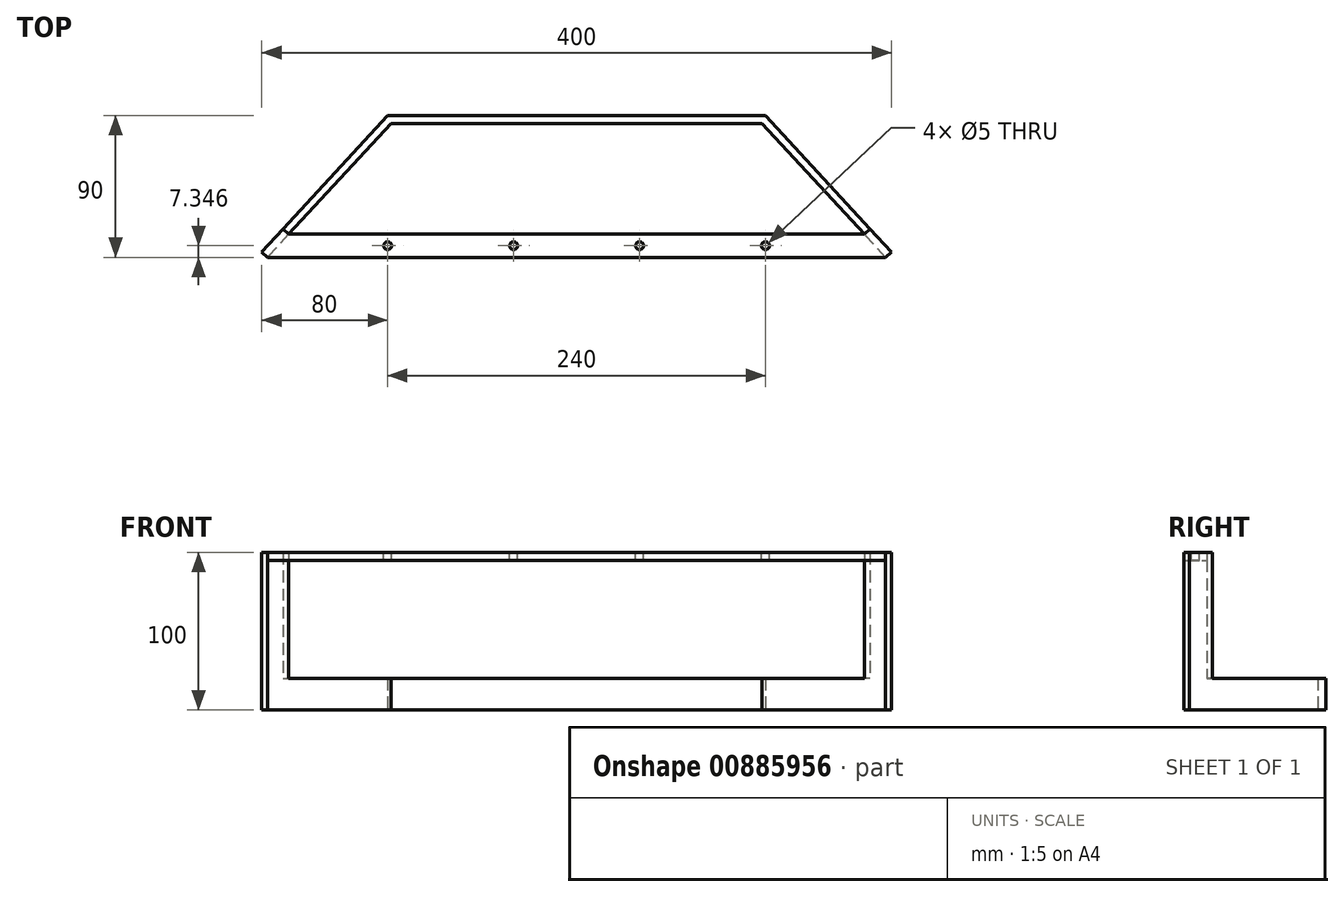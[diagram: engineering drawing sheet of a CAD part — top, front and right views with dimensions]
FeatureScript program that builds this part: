
annotation { "Feature Type Name" : "Feature", "Feature Type Description" : "" }
export const myFeature = defineFeature(function(context is Context, id is Id, definition is map)
    precondition{}
    {
        {
            var Q0;
            Q0=qCreatedBy(makeId("Top.planeOp"),FACE);
            var sketch = newSketch(context, id + "F0", { "sketchPlane" : qUnion([Q0])});
            skLineSegment(sketch, "E0", {"start": v(-200, 3.4) * mm, "end": v(-120, 90) * mm});
            skLineSegment(sketch, "E1", {"start": v(200, 3.4) * mm, "end": v(120, 90) * mm});
            skLineSegment(sketch, "E2", {"start": v(120, 90) * mm, "end": v(-120, 90) * mm});
            skLineSegment(sketch, "E3.0", {"start": v(196.33, 0) * mm, "end": v(117.81, 85) * mm});
            skLineSegment(sketch, "E3.1", {"start": v(117.81, 85) * mm, "end": v(-117.81, 85) * mm});
            skLineSegment(sketch, "E3.2", {"start": v(-196.33, 0) * mm, "end": v(-117.81, 85) * mm});
            skLineSegment(sketch, "E4", {"start": v(-196.33, 0) * mm, "end": v(-200, 3.4) * mm});
            skLineSegment(sketch, "E5", {"start": v(196.33, 0) * mm, "end": v(200, 3.4) * mm});
            skPoint(sketch, "E6.orphan", {"position": v(203.13, 0) * mm});
            skPoint(sketch, "E7.orphan", {"position": v(-203.13, 0) * mm});
            skSolve(sketch);
        }
        {
            var Q0;
            Q0 = qSketchRegion(id + "F0", true);
            extrude(context, id + "F1", {"entities" : qUnion([Q0]), "depth" : 20 * mm, "offsetDistance" : 25 * mm});
        }
        {
            var Q0;
            Q0=makeQuery(id+"F1.opExtrude","CAP_FACE",FACE,{"disambiguationData":[OSD([sQuery(id+"F0.wireOp",EDGE,"E0"),sQuery(id+"F0.wireOp",EDGE,"E1"),sQuery(id+"F0.wireOp",EDGE,"E2"),sQuery(id+"F0.wireOp",EDGE,"E3.0"),sQuery(id+"F0.wireOp",EDGE,"E3.1"),sQuery(id+"F0.wireOp",EDGE,"E3.2"),sQuery(id+"F0.wireOp",EDGE,"E4"),sQuery(id+"F0.wireOp",EDGE,"E5")])],"isStart":false});
            var sketch = newSketch(context, id + "F2", { "sketchPlane" : qUnion([Q0])});
            skLineSegment(sketch, "E8", {"start": v(-200, 3.4) * mm, "end": v(-186.43, 18.08) * mm});
            skLineSegment(sketch, "E9", {"start": v(-186.43, 18.08) * mm, "end": v(-182.76, 14.7) * mm});
            skLineSegment(sketch, "E10", {"start": v(-182.76, 14.7) * mm, "end": v(-196.33, 0) * mm});
            skLineSegment(sketch, "E11.0", {"start": v(-196.33, 0) * mm, "end": v(-200, 3.4) * mm});
            skLineSegment(sketch, "E12.MirrorCS", {"start": v(196.33, 0) * mm, "end": v(200, 3.4) * mm});
            skLineSegment(sketch, "E13.MirrorCS", {"start": v(186.43, 18.08) * mm, "end": v(182.76, 14.7) * mm});
            skLineSegment(sketch, "E14.MirrorCS", {"start": v(182.76, 14.7) * mm, "end": v(196.33, 0) * mm});
            skLineSegment(sketch, "E15.MirrorCS", {"start": v(200, 3.4) * mm, "end": v(186.43, 18.08) * mm});
            skSolve(sketch);
        }
        {
            var Q0;
            Q0=makeQuery(id+"F2.imprint","IMPRINT",FACE,{"disambiguationData":[TD([[makeQuery(id+"F2.imprint","IMPRINT",EDGE,{"derivedFrom":sQuery(id+"F2.wireOp",EDGE,"E8")}),-1.0]])]});
            var Q1;
            Q1=makeQuery(id+"F2.imprint","IMPRINT",FACE,{"disambiguationData":[TD([[makeQuery(id+"F2.imprint","IMPRINT",EDGE,{"derivedFrom":sQuery(id+"F2.wireOp",EDGE,"E12.MirrorCS")}),1.0]])]});
            extrude(context, id + "F3", {"entities" : qUnion([Q0, Q1]), "operationType" : NewBodyOperationType.ADD, "depth" : 80 * mm, "offsetDistance" : 25 * mm});
        }
        {
            var Q0;
            Q0=makeQuery(id+"F3.opExtrude","CAP_FACE",FACE,{"disambiguationData":[OSD([sQuery(id+"F2.wireOp",EDGE,"E12.MirrorCS"),sQuery(id+"F2.wireOp",EDGE,"E13.MirrorCS"),sQuery(id+"F2.wireOp",EDGE,"E14.MirrorCS"),sQuery(id+"F2.wireOp",EDGE,"E15.MirrorCS")])],"isStart":false});
            var sketch = newSketch(context, id + "F4", { "sketchPlane" : qUnion([Q0])});
            skLineSegment(sketch, "E16", {"start": v(182.76, 14.7) * mm, "end": v(-182.76, 14.7) * mm});
            skLineSegment(sketch, "E17", {"start": v(196.33, 0) * mm, "end": v(-196.33, 0) * mm});
            skLineSegment(sketch, "E18", {"start": v(-182.76, 14.7) * mm, "end": v(-196.33, 0) * mm});
            skLineSegment(sketch, "E19", {"start": v(182.76, 14.7) * mm, "end": v(196.33, 0) * mm});
            skLineSegment(sketch, "E20", {"start": v(-189.54, 7.35) * mm, "end": v(189.54, 7.35) * mm, "construction": true});
            skPoint(sketch, "E20.startSnap0", {"position": v(-189.54, 7.35) * mm});
            skCircle(sketch, "E21", {"center": v(-40, 7.35) * mm, "radius": 2.5 * mm});
            skCircle(sketch, "E22", {"center": v(-120, 7.35) * mm, "radius": 2.5 * mm});
            skCircle(sketch, "E23.MirrorC", {"center": v(120, 7.35) * mm, "radius": 2.5 * mm});
            skCircle(sketch, "E24.MirrorC", {"center": v(40, 7.35) * mm, "radius": 2.5 * mm});
            skSolve(sketch);
        }
        {
            var Q0;
            Q0 = qSketchRegion(id + "F4", true);
            extrude(context, id + "F5", {"entities" : qUnion([Q0]), "operationType" : NewBodyOperationType.ADD, "oppositeDirection" : true, "depth" : 5 * mm, "offsetDistance" : 25 * mm});
        }
    });
